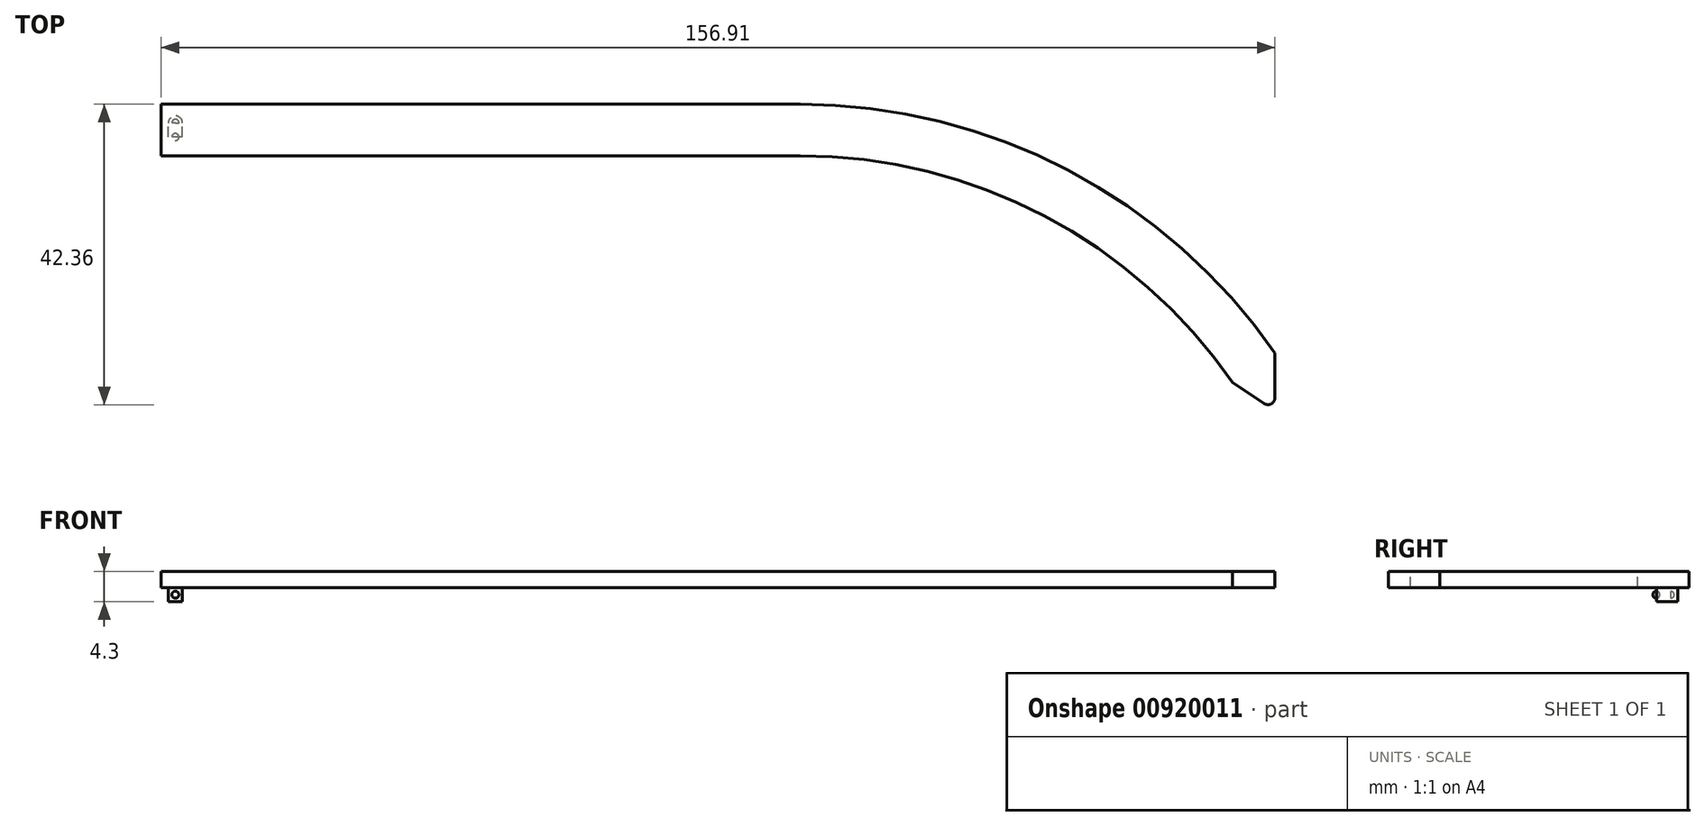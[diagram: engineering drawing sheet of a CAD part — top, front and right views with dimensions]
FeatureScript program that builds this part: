
annotation { "Feature Type Name" : "Feature", "Feature Type Description" : "" }
export const myFeature = defineFeature(function(context is Context, id is Id, definition is map)
    precondition{}
    {
        {
            var Q0;
            Q0=qCreatedBy(makeId("Top.planeOp"),FACE);
            var sketch = newSketch(context, id + "F0", { "sketchPlane" : qUnion([Q0])});
            skLineSegment(sketch, "E0.bottom", {"start": v(-45, 3.62) * mm, "end": v(45, 3.62) * mm});
            skLineSegment(sketch, "E0.top", {"start": v(-45, -3.62) * mm, "end": v(45, -3.62) * mm});
            skLineSegment(sketch, "E0.left", {"start": v(-45, 3.62) * mm, "end": v(-45, -3.62) * mm});
            skLineSegment(sketch, "E0.right", {"start": v(45, 3.62) * mm, "end": v(45, -3.62) * mm});
            skPoint(sketch, "E0.middle", {"position": v(0, 0) * mm});
            skLineSegment(sketch, "E1", {"start": v(45, 20.51) * mm, "end": v(45, -38.93) * mm});
            skArc(sketch, "E2", {"start": v(111.91, -31.5) * mm, "mid": v(82.79, -5.69) * mm, "end": v(45, 3.62) * mm});
            skArc(sketch, "E3.0", {"start": v(105.95, -35.62) * mm, "mid": v(79.42, -12.1) * mm, "end": v(45, -3.62) * mm});
            skLineSegment(sketch, "E4", {"start": v(105.95, -35.62) * mm, "end": v(110.36, -38.57) * mm});
            skLineSegment(sketch, "E5", {"start": v(111.91, -37.75) * mm, "end": v(111.91, -31.5) * mm});
            skPoint(sketch, "E6.visualSharp", {"position": v(111.91, -39.62) * mm});
            skArc(sketch, "E6.filletArc", {"start": v(110.36, -38.57) * mm, "mid": v(111.39, -38.63) * mm, "end": v(111.91, -37.75) * mm});
            skLineSegment(sketch, "E7", {"start": v(-45, 0) * mm, "end": v(-44, 0) * mm});
            skLineSegment(sketch, "E8", {"start": v(-44, 0) * mm, "end": v(-43, 0) * mm});
            skLineSegment(sketch, "E9.bottom", {"start": v(-42, 1) * mm, "end": v(-44, 1) * mm});
            skLineSegment(sketch, "E9.top", {"start": v(-42, -1) * mm, "end": v(-44, -1) * mm});
            skLineSegment(sketch, "E9.left", {"start": v(-42, 1) * mm, "end": v(-42, -1) * mm});
            skLineSegment(sketch, "E9.right", {"start": v(-44, 1) * mm, "end": v(-44, -1) * mm});
            skPoint(sketch, "E9.middle", {"position": v(-43, 0) * mm});
            skSolve(sketch);
        }
        {
            var Q0;
            {var subQ6=sQuery(id+"F0.wireOp",EDGE,"E0.bottom");Q0=makeQuery(id+"F0.imprint","IMPRINT",FACE,{"disambiguationData":[TD([[makeQuery(id+"F0.imprint","IMPRINT",EDGE,{"derivedFrom":subQ6}),-1.0]])]});}
            var Q1;
            Q1=makeQuery(id+"F0.imprint","IMPRINT",FACE,{"disambiguationData":[TD([[makeQuery(id+"F0.imprint","IMPRINT",EDGE,{"derivedFrom":sQuery(id+"F0.wireOp",EDGE,"E0.right")}),1.0]])]});
            var Q2;
            {var subQ3=sQuery(id+"F0.wireOp",EDGE,"E9.bottom");Q2=makeQuery(id+"F0.imprint","IMPRINT",FACE,{"disambiguationData":[TD([[makeQuery(id+"F0.imprint","IMPRINT",EDGE,{"derivedFrom":subQ3}),1.0]])]});}
            extrude(context, id + "F1", {"entities" : qUnion([Q0, Q1, Q2]), "oppositeDirection" : true, "depth" : 2.3 * mm, "offsetDistance" : 25 * mm});
        }
        {
            var Q0;
            Q0=makeQuery(id+"F1.opExtrude","CAP_FACE",FACE,{"disambiguationData":[OSD([sQuery(id+"F0.wireOp",EDGE,"E0.bottom"),sQuery(id+"F0.wireOp",EDGE,"E0.top"),sQuery(id+"F0.wireOp",EDGE,"E0.left"),sQuery(id+"F0.wireOp",EDGE,"E2"),sQuery(id+"F0.wireOp",EDGE,"E3.0"),sQuery(id+"F0.wireOp",EDGE,"E4"),sQuery(id+"F0.wireOp",EDGE,"E5"),sQuery(id+"F0.wireOp",EDGE,"E6.filletArc")])],"isStart":false});
            var sketch = newSketch(context, id + "F2", { "sketchPlane" : qUnion([Q0])});
            skLineSegment(sketch, "E10", {"start": v(-45, 0) * mm, "end": v(-43, 0) * mm});
            skLineSegment(sketch, "E11.bottom", {"start": v(-42, 1) * mm, "end": v(-44, 1) * mm});
            skLineSegment(sketch, "E11.top", {"start": v(-42, -1) * mm, "end": v(-44, -1) * mm});
            skLineSegment(sketch, "E11.left", {"start": v(-42, 1) * mm, "end": v(-42, -1) * mm});
            skLineSegment(sketch, "E11.right", {"start": v(-44, 1) * mm, "end": v(-44, -1) * mm});
            skPoint(sketch, "E11.middle", {"position": v(-43, 0) * mm});
            skSolve(sketch);
        }
        {
            var Q0;
            {var subQ1=sQuery(id+"F2.wireOp",EDGE,"E11.bottom");Q0=makeQuery(id+"F2.imprint","IMPRINT",FACE,{"disambiguationData":[TD([[makeQuery(id+"F2.imprint","IMPRINT",EDGE,{"derivedFrom":subQ1}),1.0]])]});}
            extrude(context, id + "F3", {"entities" : qUnion([Q0]), "operationType" : NewBodyOperationType.ADD, "depth" : 2 * mm, "offsetDistance" : 25 * mm});
        }
        {
            var Q0;
            Q0=makeQuery(id+"F3.opExtrude","SWEPT_FACE",FACE,{"disambiguationData":[OSD([sQuery(id+"F2.wireOp",EDGE,"E11.bottom")])]});
            var sketch = newSketch(context, id + "F4", { "sketchPlane" : qUnion([Q0])});
            skLineSegment(sketch, "E12", {"start": v(-42, -3.3) * mm, "end": v(-44, -3.3) * mm});
            skLineSegment(sketch, "E13", {"start": v(-43, -2.3) * mm, "end": v(-43, -4.3) * mm});
            skArc(sketch, "E14", {"start": v(-43, -2.8) * mm, "mid": v(-42.5, -3.3) * mm, "end": v(-43, -3.8) * mm});
            skSolve(sketch);
        }
        {
            var Q0;
            {var subQ0=sQuery(id+"F4.wireOp",EDGE,"E14");var subQ1=sQuery(id+"F4.wireOp",EDGE,"E12");var subQ2=makeQuery(id+"F4.imprint","INTERSECT",VERTEX,{"derivedFrom":[subQ1,subQ0]});Q0=makeQuery(id+"F4.imprint","IMPRINT",FACE,{"disambiguationData":[TD([[makeQuery(id+"F4.imprint","IMPRINT",EDGE,{"disambiguationData":[TD([[subQ2,-1.0]])],"derivedFrom":subQ1}),-1.0]])]});}
            var Q1;
            {var subQ0=sQuery(id+"F4.wireOp",EDGE,"E14");var subQ1=sQuery(id+"F4.wireOp",EDGE,"E12");var subQ2=makeQuery(id+"F4.imprint","INTERSECT",VERTEX,{"derivedFrom":[subQ1,subQ0]});Q1=makeQuery(id+"F4.imprint","IMPRINT",FACE,{"disambiguationData":[TD([[makeQuery(id+"F4.imprint","IMPRINT",EDGE,{"disambiguationData":[TD([[subQ2,-1.0]])],"derivedFrom":subQ1}),1.0]])]});}
            var Q2;
            Q2=sQuery(id+"F4.wireOp",EDGE,"E13");
            revolve(context, id + "F5", {"surfaceOperationType" : NewSurfaceOperationType.NEW, "entities" : qUnion([Q0, Q1]), "axis" : qUnion([Q2]), "revolveType" : RevolveType.FULL});
        }
        {
            var Q0;
            Q0=makeQuery(id+"F3.opExtrude","SWEPT_FACE",FACE,{"disambiguationData":[OSD([sQuery(id+"F2.wireOp",EDGE,"E11.top")])]});
            var sketch = newSketch(context, id + "F6", { "sketchPlane" : qUnion([Q0])});
            skLineSegment(sketch, "E15", {"start": v(43, -2.3) * mm, "end": v(43, -4.3) * mm});
            skLineSegment(sketch, "E16", {"start": v(42, -3.3) * mm, "end": v(44, -3.3) * mm});
            skArc(sketch, "E17", {"start": v(43, -2.8) * mm, "mid": v(43.5, -3.3) * mm, "end": v(43, -3.8) * mm});
            skSolve(sketch);
        }
        {
            var Q0;
            {var subQ0=sQuery(id+"F6.wireOp",EDGE,"E17");var subQ1=sQuery(id+"F6.wireOp",EDGE,"E15");var subQ2=makeQuery(id+"F6.imprint","INTERSECT",VERTEX,{"disambiguationData":[OD(0.0)],"derivedFrom":[subQ1,subQ0]});Q0=makeQuery(id+"F6.imprint","IMPRINT",FACE,{"disambiguationData":[TD([[makeQuery(id+"F6.imprint","IMPRINT",EDGE,{"disambiguationData":[TD([[subQ2,-1.0]])],"derivedFrom":subQ1}),1.0]])]});}
            var Q1;
            {var subQ0=sQuery(id+"F6.wireOp",EDGE,"E17");var subQ1=sQuery(id+"F6.wireOp",EDGE,"E15");var subQ2=makeQuery(id+"F6.imprint","INTERSECT",VERTEX,{"disambiguationData":[OD(1.0)],"derivedFrom":[subQ1,subQ0]});Q1=makeQuery(id+"F6.imprint","IMPRINT",FACE,{"disambiguationData":[TD([[makeQuery(id+"F6.imprint","IMPRINT",EDGE,{"disambiguationData":[TD([[subQ2,1.0]])],"derivedFrom":subQ1}),1.0]])]});}
            var Q2;
            Q2=sQuery(id+"F6.wireOp",EDGE,"E15");
            revolve(context, id + "F7", {"operationType" : NewBodyOperationType.ADD, "surfaceOperationType" : NewSurfaceOperationType.NEW, "entities" : qUnion([Q0, Q1]), "axis" : qUnion([Q2]), "revolveType" : RevolveType.FULL});
        }
    });
